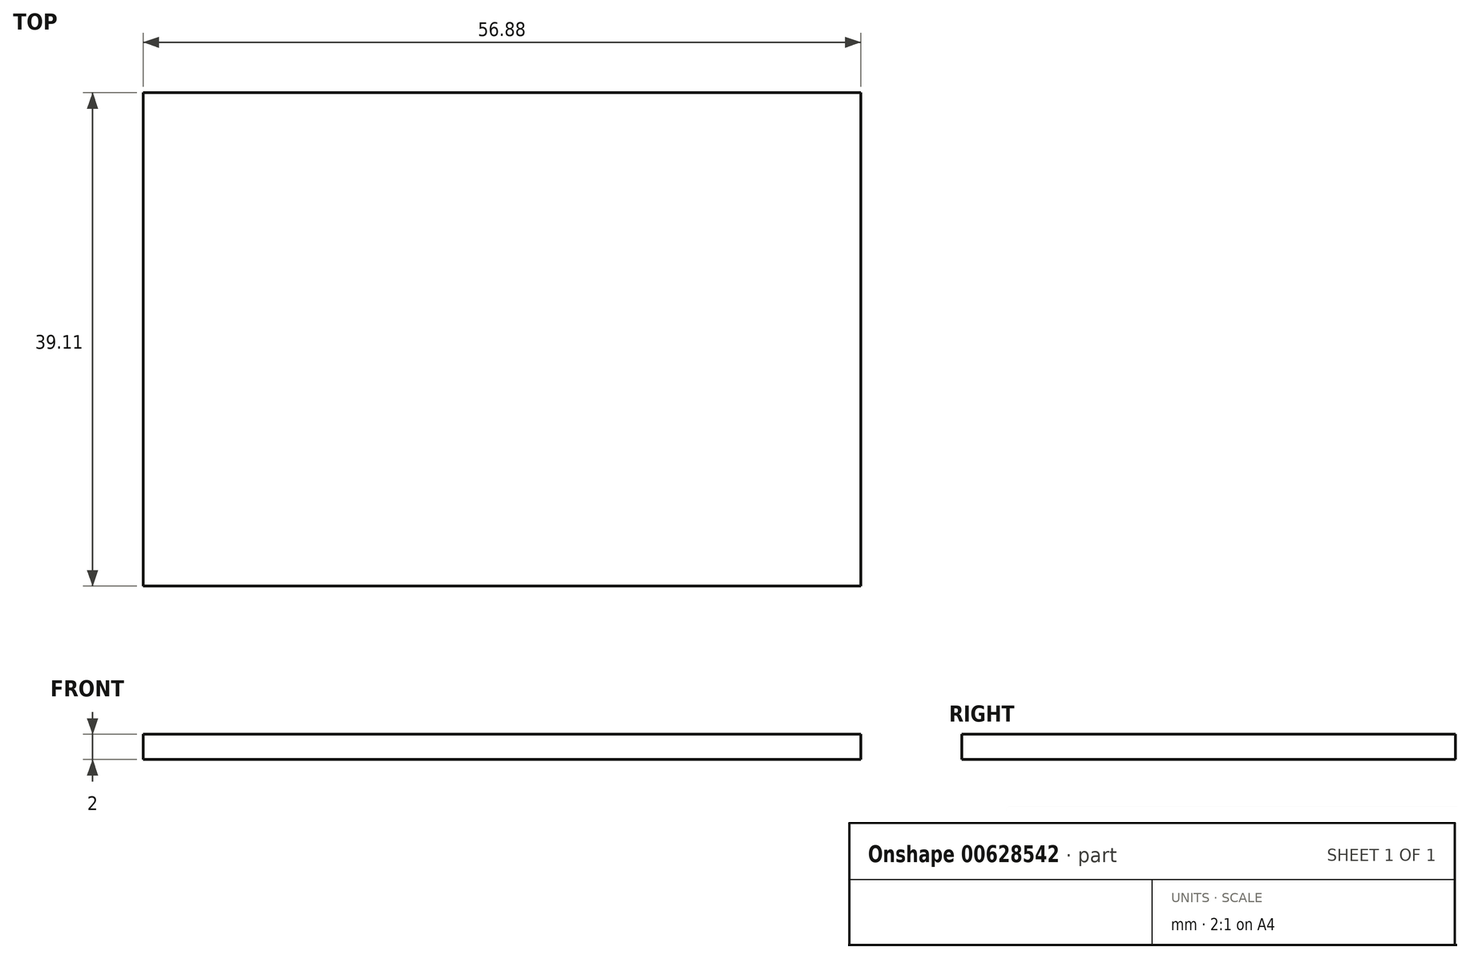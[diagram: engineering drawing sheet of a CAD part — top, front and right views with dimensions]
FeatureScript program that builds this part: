
annotation { "Feature Type Name" : "Feature", "Feature Type Description" : "" }
export const myFeature = defineFeature(function(context is Context, id is Id, definition is map)
    precondition{}
    {
        {
            var Q0;
            Q0=qCreatedBy(makeId("Top.planeOp"),FACE);
            var sketch = newSketch(context, id + "F0", { "sketchPlane" : qUnion([Q0])});
            skLineSegment(sketch, "E0.bottom", {"start": v(0, 0) * mm, "end": v(56.88, 0) * mm});
            skLineSegment(sketch, "E0.top", {"start": v(0, 39.1) * mm, "end": v(56.88, 39.1) * mm});
            skLineSegment(sketch, "E0.left", {"start": v(0, 0) * mm, "end": v(0, 39.1) * mm});
            skLineSegment(sketch, "E0.right", {"start": v(56.88, 0) * mm, "end": v(56.88, 39.1) * mm});
            skSolve(sketch);
        }
        {
            var Q0;
            Q0=makeQuery(id+"F0.imprint","IMPRINT",FACE,{"disambiguationData":[TD([[makeQuery(id+"F0.imprint","IMPRINT",EDGE,{"derivedFrom":sQuery(id+"F0.wireOp",EDGE,"E0.bottom")}),1.0]])]});
            extrude(context, id + "F1", {"entities" : qUnion([Q0]), "depth" : 2 * mm, "offsetDistance" : 25 * mm});
        }
    });
